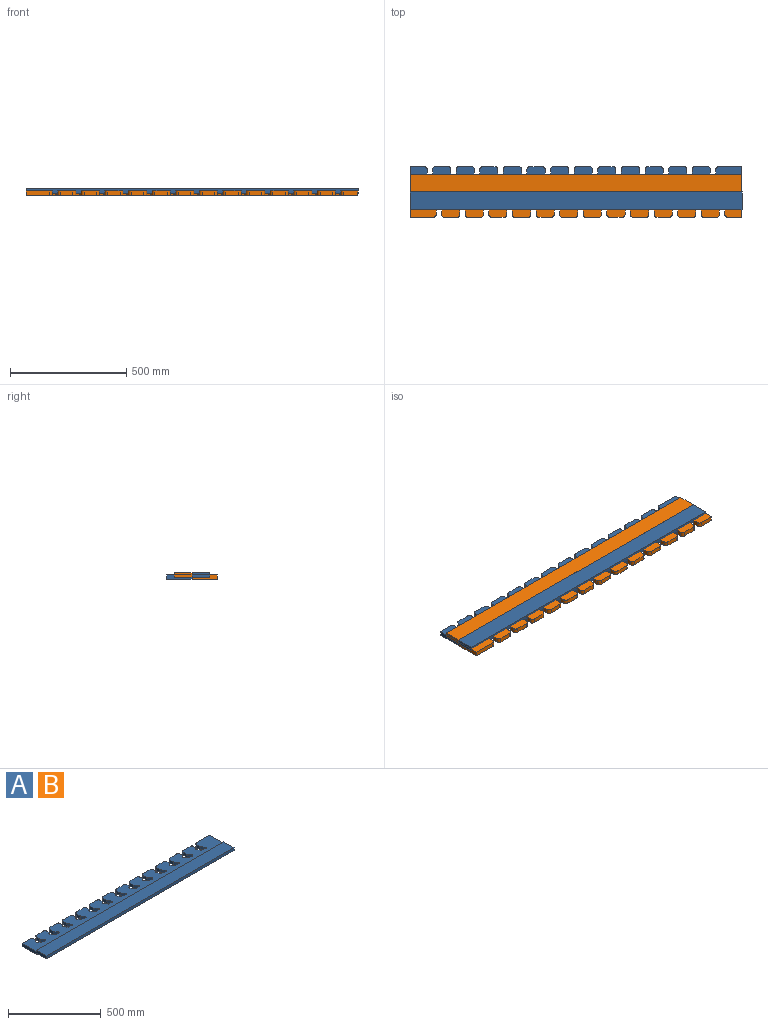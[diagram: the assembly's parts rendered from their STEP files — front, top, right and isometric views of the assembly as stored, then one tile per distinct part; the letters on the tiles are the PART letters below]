
ASSEMBLY  parts=2 mates=1
PART A: 208 faces, bbox 1428.8x185.4x28.6 mm
  f0: plane 52.88x19.05mm, normal (0,1,0), area 1007.4mm2, adj f1,f200,f201,f202
  f1: cylinder r=12.7mm len=19.05mm, axis (0,0,-1), area 380mm2, adj f0,f2,f201,f202
  f2: plane 25.53x19.05mm, normal (-1,0,0), area 486.4mm2, adj f1,f3,f201,f202
  f3: cylinder r=5.08mm len=19.05mm, axis (0,0,-1), area 70mm2, adj f2,f4,f201,f202
  f4: cylinder r=6.35mm len=19.05mm, axis (0,0,-1), area 12.4mm2, adj f3,f5,f201,f202
  f5: plane 20.02x19.05mm, normal (-0.81,-0.58,0), area 468.9mm2, adj f4,f6,f201,f202
  f6: cylinder r=6.35mm len=19.05mm, axis (0,0,-1), area 277mm2, adj f5,f7,f201,f202
  f7: plane 26.38x19.05mm, normal (0.1,1,0), area 504.9mm2, adj f6,f8,f201,f202
  f8: cylinder r=2.19mm len=19.05mm, axis (0,0,-1), area 35.6mm2, adj f7,f9,f201,f202
  f9: plane 21.55x19.05mm, normal (0.81,0.58,0), area 504.9mm2, adj f8,f10,f201,f202
  f10: cylinder r=6.35mm len=19.05mm, axis (0,0,-1), area 277mm2, adj f9,f11,f201,f202
  f11: plane 19.05x1.53mm, normal (0.1,1,0), area 29.2mm2, adj f10,f12,f201,f202
  f12: cylinder r=5.08mm len=19.05mm, axis (0,0,-1), area 161.5mm2, adj f11,f13,f201,f202
  f13: plane 19.18x19.05mm, normal (1,0,0), area 365.3mm2, adj f12,f14,f201,f202
  f14: cylinder r=12.7mm len=19.05mm, axis (0,0,-1), area 380mm2, adj f13,f15,f201,f202
  f15: plane 60.96x19.05mm, normal (0,1,0), area 1161.2mm2, adj f14,f16,f201,f202
  f16: plane 185.42x28.58mm, normal (-1,0,0), area 3532.3mm2, adj f15,f17,f201,f202,f203,f204,f206,f207
  f17: plane 1428.75x9.53mm, normal (0,-1,0), area 13608.8mm2, adj f16,f18,f202,f207
  f18: plane 109.22x19.05mm, normal (1,0,0), area 2080.6mm2, adj f17,f19,f201,f202,f203
  f19: plane 99.88x19.05mm, normal (0,1,0), area 1902.7mm2, adj f18,f20,f201,f202
  f20: cylinder r=12.7mm len=19.05mm, axis (0,0,-1), area 380mm2, adj f19,f21,f201,f202
  f21: plane 25.53x19.05mm, normal (-1,0,0), area 486.4mm2, adj f20,f22,f201,f202
  f22: cylinder r=5.08mm len=19.05mm, axis (0,0,-1), area 70mm2, adj f21,f23,f201,f202
  f23: cylinder r=6.35mm len=19.05mm, axis (0,0,-1), area 12.4mm2, adj f22,f24,f201,f202
  f24: plane 20.02x19.05mm, normal (-0.81,-0.58,0), area 468.9mm2, adj f23,f25,f201,f202
  f25: cylinder r=6.35mm len=19.05mm, axis (0,0,-1), area 277mm2, adj f24,f26,f201,f202
  f26: plane 26.38x19.05mm, normal (0.1,1,0), area 504.9mm2, adj f25,f27,f201,f202
  f27: cylinder r=2.19mm len=19.05mm, axis (0,0,-1), area 35.6mm2, adj f26,f28,f201,f202
  f28: plane 21.55x19.05mm, normal (0.81,0.58,0), area 504.9mm2, adj f27,f29,f201,f202
  f29: cylinder r=6.35mm len=19.05mm, axis (0,0,-1), area 277mm2, adj f28,f30,f201,f202
  f30: plane 19.05x1.53mm, normal (0.1,1,0), area 29.2mm2, adj f29,f31,f201,f202
  f31: cylinder r=5.08mm len=19.05mm, axis (0,0,-1), area 161.5mm2, adj f30,f32,f201,f202
  f32: plane 19.18x19.05mm, normal (1,0,0), area 365.3mm2, adj f31,f33,f201,f202
  f33: cylinder r=12.7mm len=19.05mm, axis (0,0,-1), area 380mm2, adj f32,f34,f201,f202
  f34: plane 52.88x19.05mm, normal (0,1,0), area 1007.4mm2, adj f33,f35,f201,f202
  f35: cylinder r=12.7mm len=19.05mm, axis (0,0,-1), area 380mm2, adj f34,f36,f201,f202
  f36: plane 25.53x19.05mm, normal (-1,0,0), area 486.4mm2, adj f35,f37,f201,f202
  f37: cylinder r=5.08mm len=19.05mm, axis (0,0,-1), area 70mm2, adj f36,f38,f201,f202
  f38: cylinder r=6.35mm len=19.05mm, axis (0,0,-1), area 12.4mm2, adj f37,f39,f201,f202
  f39: plane 20.02x19.05mm, normal (-0.81,-0.58,0), area 468.9mm2, adj f38,f40,f201,f202
  f40: cylinder r=6.35mm len=19.05mm, axis (0,0,-1), area 277mm2, adj f39,f41,f201,f202
  f41: plane 26.38x19.05mm, normal (0.1,1,0), area 504.9mm2, adj f40,f42,f201,f202
  f42: cylinder r=2.19mm len=19.05mm, axis (0,0,-1), area 35.6mm2, adj f41,f43,f201,f202
  f43: plane 21.55x19.05mm, normal (0.81,0.58,0), area 504.9mm2, adj f42,f44,f201,f202
  f44: cylinder r=6.35mm len=19.05mm, axis (0,0,-1), area 277mm2, adj f43,f45,f201,f202
  f45: plane 19.05x1.53mm, normal (0.1,1,0), area 29.2mm2, adj f44,f46,f201,f202
  f46: cylinder r=5.08mm len=19.05mm, axis (0,0,-1), area 161.5mm2, adj f45,f47,f201,f202
  f47: plane 19.18x19.05mm, normal (1,0,0), area 365.3mm2, adj f46,f48,f201,f202
  f48: cylinder r=12.7mm len=19.05mm, axis (0,0,-1), area 380mm2, adj f47,f49,f201,f202
  f49: plane 52.88x19.05mm, normal (0,1,0), area 1007.4mm2, adj f48,f50,f201,f202
  f50: cylinder r=12.7mm len=19.05mm, axis (0,0,-1), area 380mm2, adj f49,f51,f201,f202
  f51: plane 25.53x19.05mm, normal (-1,0,0), area 486.4mm2, adj f50,f52,f201,f202
  f52: cylinder r=5.08mm len=19.05mm, axis (0,0,-1), area 70mm2, adj f51,f53,f201,f202
  f53: cylinder r=6.35mm len=19.05mm, axis (0,0,-1), area 12.4mm2, adj f52,f54,f201,f202
  f54: plane 20.02x19.05mm, normal (-0.81,-0.58,0), area 468.9mm2, adj f53,f55,f201,f202
  f55: cylinder r=6.35mm len=19.05mm, axis (0,0,-1), area 277mm2, adj f54,f56,f201,f202
  f56: plane 26.38x19.05mm, normal (0.1,1,0), area 504.9mm2, adj f55,f57,f201,f202
  f57: cylinder r=2.19mm len=19.05mm, axis (0,0,-1), area 35.6mm2, adj f56,f58,f201,f202
  f58: plane 21.55x19.05mm, normal (0.81,0.58,0), area 504.9mm2, adj f57,f59,f201,f202
  f59: cylinder r=6.35mm len=19.05mm, axis (0,0,-1), area 277mm2, adj f58,f60,f201,f202
  f60: plane 19.05x1.53mm, normal (0.1,1,0), area 29.2mm2, adj f59,f61,f201,f202
  f61: cylinder r=5.08mm len=19.05mm, axis (0,0,-1), area 161.5mm2, adj f60,f62,f201,f202
  f62: plane 19.18x19.05mm, normal (1,0,0), area 365.3mm2, adj f61,f63,f201,f202
  f63: cylinder r=12.7mm len=19.05mm, axis (0,0,-1), area 380mm2, adj f62,f64,f201,f202
  f64: plane 52.88x19.05mm, normal (0,1,0), area 1007.4mm2, adj f63,f65,f201,f202
  f65: cylinder r=12.7mm len=19.05mm, axis (0,0,-1), area 380mm2, adj f64,f66,f201,f202
  f66: plane 25.53x19.05mm, normal (-1,0,0), area 486.4mm2, adj f65,f67,f201,f202
  f67: cylinder r=5.08mm len=19.05mm, axis (0,0,-1), area 70mm2, adj f66,f68,f201,f202
  f68: cylinder r=6.35mm len=19.05mm, axis (0,0,-1), area 12.4mm2, adj f67,f69,f201,f202
  f69: plane 20.02x19.05mm, normal (-0.81,-0.58,0), area 468.9mm2, adj f68,f70,f201,f202
  f70: cylinder r=6.35mm len=19.05mm, axis (0,0,-1), area 277mm2, adj f69,f71,f201,f202
  f71: plane 26.38x19.05mm, normal (0.1,1,0), area 504.9mm2, adj f70,f72,f201,f202
  f72: cylinder r=2.19mm len=19.05mm, axis (0,0,-1), area 35.6mm2, adj f71,f73,f201,f202
  f73: plane 21.55x19.05mm, normal (0.81,0.58,0), area 504.9mm2, adj f72,f74,f201,f202
  f74: cylinder r=6.35mm len=19.05mm, axis (0,0,-1), area 277mm2, adj f73,f75,f201,f202
  f75: plane 19.05x1.53mm, normal (0.1,1,0), area 29.2mm2, adj f74,f76,f201,f202
  f76: cylinder r=5.08mm len=19.05mm, axis (0,0,-1), area 161.5mm2, adj f75,f77,f201,f202
  f77: plane 19.18x19.05mm, normal (1,0,0), area 365.3mm2, adj f76,f78,f201,f202
  f78: cylinder r=12.7mm len=19.05mm, axis (0,0,-1), area 380mm2, adj f77,f79,f201,f202
  f79: plane 52.88x19.05mm, normal (0,1,0), area 1007.4mm2, adj f78,f80,f201,f202
  f80: cylinder r=12.7mm len=19.05mm, axis (0,0,-1), area 380mm2, adj f79,f81,f201,f202
  f81: plane 25.53x19.05mm, normal (-1,0,0), area 486.4mm2, adj f80,f82,f201,f202
  f82: cylinder r=5.08mm len=19.05mm, axis (0,0,-1), area 70mm2, adj f81,f83,f201,f202
  f83: cylinder r=6.35mm len=19.05mm, axis (0,0,-1), area 12.4mm2, adj f82,f84,f201,f202
  f84: plane 20.02x19.05mm, normal (-0.81,-0.58,0), area 468.9mm2, adj f83,f85,f201,f202
  f85: cylinder r=6.35mm len=19.05mm, axis (0,0,-1), area 277mm2, adj f84,f86,f201,f202
  f86: plane 26.38x19.05mm, normal (0.1,1,0), area 504.9mm2, adj f85,f87,f201,f202
  f87: cylinder r=2.19mm len=19.05mm, axis (0,0,-1), area 35.6mm2, adj f86,f88,f201,f202
  f88: plane 21.55x19.05mm, normal (0.81,0.58,0), area 504.9mm2, adj f87,f89,f201,f202
  f89: cylinder r=6.35mm len=19.05mm, axis (0,0,-1), area 277mm2, adj f88,f90,f201,f202
  f90: plane 19.05x1.53mm, normal (0.1,1,0), area 29.2mm2, adj f89,f91,f201,f202
  f91: cylinder r=5.08mm len=19.05mm, axis (0,0,-1), area 161.5mm2, adj f90,f92,f201,f202
  f92: plane 19.18x19.05mm, normal (1,0,0), area 365.3mm2, adj f91,f93,f201,f202
  f93: cylinder r=12.7mm len=19.05mm, axis (0,0,-1), area 380mm2, adj f92,f94,f201,f202
  f94: plane 52.88x19.05mm, normal (0,1,0), area 1007.4mm2, adj f93,f95,f201,f202
  f95: cylinder r=12.7mm len=19.05mm, axis (0,0,-1), area 380mm2, adj f94,f96,f201,f202
  f96: plane 25.53x19.05mm, normal (-1,0,0), area 486.4mm2, adj f95,f97,f201,f202
  f97: cylinder r=5.08mm len=19.05mm, axis (0,0,-1), area 70mm2, adj f96,f98,f201,f202
  f98: cylinder r=6.35mm len=19.05mm, axis (0,0,-1), area 12.4mm2, adj f97,f99,f201,f202
  f99: plane 20.02x19.05mm, normal (-0.81,-0.58,0), area 468.9mm2, adj f98,f100,f201,f202
  f100: cylinder r=6.35mm len=19.05mm, axis (0,0,-1), area 277mm2, adj f99,f101,f201,f202
  f101: plane 26.38x19.05mm, normal (0.1,1,0), area 504.9mm2, adj f100,f102,f201,f202
  f102: cylinder r=2.19mm len=19.05mm, axis (0,0,-1), area 35.6mm2, adj f101,f103,f201,f202
  f103: plane 21.55x19.05mm, normal (0.81,0.58,0), area 504.9mm2, adj f102,f104,f201,f202
  f104: cylinder r=6.35mm len=19.05mm, axis (0,0,-1), area 277mm2, adj f103,f105,f201,f202
  f105: plane 19.05x1.53mm, normal (0.1,1,0), area 29.2mm2, adj f104,f106,f201,f202
  f106: cylinder r=5.08mm len=19.05mm, axis (0,0,-1), area 161.5mm2, adj f105,f107,f201,f202
  f107: plane 19.18x19.05mm, normal (1,0,0), area 365.3mm2, adj f106,f108,f201,f202
  f108: cylinder r=12.7mm len=19.05mm, axis (0,0,-1), area 380mm2, adj f107,f109,f201,f202
  f109: plane 52.88x19.05mm, normal (0,1,0), area 1007.4mm2, adj f108,f110,f201,f202
  f110: cylinder r=12.7mm len=19.05mm, axis (0,0,-1), area 380mm2, adj f109,f111,f201,f202
  f111: plane 25.53x19.05mm, normal (-1,0,0), area 486.4mm2, adj f110,f112,f201,f202
  f112: cylinder r=5.08mm len=19.05mm, axis (0,0,-1), area 70mm2, adj f111,f113,f201,f202
  f113: cylinder r=6.35mm len=19.05mm, axis (0,0,-1), area 12.4mm2, adj f112,f114,f201,f202
  f114: plane 20.02x19.05mm, normal (-0.81,-0.58,0), area 468.9mm2, adj f113,f115,f201,f202
  f115: cylinder r=6.35mm len=19.05mm, axis (0,0,-1), area 277mm2, adj f114,f116,f201,f202
  f116: plane 26.38x19.05mm, normal (0.1,1,0), area 504.9mm2, adj f115,f117,f201,f202
  f117: cylinder r=2.19mm len=19.05mm, axis (0,0,-1), area 35.6mm2, adj f116,f118,f201,f202
  f118: plane 21.55x19.05mm, normal (0.81,0.58,0), area 504.9mm2, adj f117,f119,f201,f202
  f119: cylinder r=6.35mm len=19.05mm, axis (0,0,-1), area 277mm2, adj f118,f120,f201,f202
  f120: plane 19.05x1.53mm, normal (0.1,1,0), area 29.2mm2, adj f119,f121,f201,f202
  f121: cylinder r=5.08mm len=19.05mm, axis (0,0,-1), area 161.5mm2, adj f120,f122,f201,f202
  f122: plane 19.18x19.05mm, normal (1,0,0), area 365.3mm2, adj f121,f123,f201,f202
  f123: extruded ~19.05x7.08mm, area 141.2mm2, adj f122,f124,f201,f202
  f124: cylinder r=12.7mm len=19.05mm, axis (0,0,-1), area 229.2mm2, adj f123,f125,f201,f202
  f125: extruded ~19.05x0.41mm, area 7.7mm2, adj f124,f126,f201,f202
  f126: plane 52.88x19.05mm, normal (0,1,0), area 1007.4mm2, adj f125,f127,f201,f202
  f127: cylinder r=12.7mm len=19.05mm, axis (0,0,-1), area 380mm2, adj f126,f128,f201,f202
  f128: plane 25.53x19.05mm, normal (-1,0,0), area 486.4mm2, adj f127,f129,f201,f202
  f129: cylinder r=5.08mm len=19.05mm, axis (0,0,-1), area 70mm2, adj f128,f130,f201,f202
  f130: cylinder r=6.35mm len=19.05mm, axis (0,0,-1), area 12.4mm2, adj f129,f131,f201,f202
  f131: plane 20.02x19.05mm, normal (-0.81,-0.58,0), area 468.9mm2, adj f130,f132,f201,f202
  f132: cylinder r=6.35mm len=19.05mm, axis (0,0,-1), area 277mm2, adj f131,f133,f201,f202
  f133: plane 26.38x19.05mm, normal (0.1,1,0), area 504.9mm2, adj f132,f134,f201,f202
  f134: cylinder r=2.19mm len=19.05mm, axis (0,0,-1), area 35.6mm2, adj f133,f135,f201,f202
  f135: plane 21.55x19.05mm, normal (0.81,0.58,0), area 504.9mm2, adj f134,f136,f201,f202
  f136: cylinder r=6.35mm len=19.05mm, axis (0,0,-1), area 277mm2, adj f135,f137,f201,f202
  f137: plane 19.05x1.53mm, normal (0.1,1,0), area 29.2mm2, adj f136,f138,f201,f202
  f138: cylinder r=5.08mm len=19.05mm, axis (0,0,-1), area 161.5mm2, adj f137,f139,f201,f202
  f139: plane 19.18x19.05mm, normal (1,0,0), area 365.3mm2, adj f138,f140,f201,f202
  f140: cylinder r=12.7mm len=19.05mm, axis (0,0,-1), area 380mm2, adj f139,f141,f201,f202
  f141: plane 52.88x19.05mm, normal (0,1,0), area 1007.4mm2, adj f140,f142,f201,f202
  f142: cylinder r=12.7mm len=19.05mm, axis (0,0,-1), area 380mm2, adj f141,f143,f201,f202
  f143: plane 25.53x19.05mm, normal (-1,0,0), area 486.4mm2, adj f142,f144,f201,f202
  f144: cylinder r=5.08mm len=19.05mm, axis (0,0,-1), area 70mm2, adj f143,f145,f201,f202
  f145: cylinder r=6.35mm len=19.05mm, axis (0,0,-1), area 12.4mm2, adj f144,f146,f201,f202
  f146: plane 20.02x19.05mm, normal (-0.81,-0.58,0), area 468.9mm2, adj f145,f147,f201,f202
  f147: cylinder r=6.35mm len=19.05mm, axis (0,0,-1), area 277mm2, adj f146,f148,f201,f202
  f148: plane 26.38x19.05mm, normal (0.1,1,0), area 504.9mm2, adj f147,f149,f201,f202
  f149: cylinder r=2.19mm len=19.05mm, axis (0,0,-1), area 35.6mm2, adj f148,f150,f201,f202
  f150: plane 21.55x19.05mm, normal (0.81,0.58,0), area 504.9mm2, adj f149,f151,f201,f202
  f151: cylinder r=6.35mm len=19.05mm, axis (0,0,-1), area 277mm2, adj f150,f152,f201,f202
  f152: plane 19.05x1.53mm, normal (0.1,1,0), area 29.2mm2, adj f151,f153,f201,f202
  f153: cylinder r=5.08mm len=19.05mm, axis (0,0,-1), area 161.5mm2, adj f152,f154,f201,f202
  f154: plane 19.18x19.05mm, normal (1,0,0), area 365.3mm2, adj f153,f155,f201,f202
  f155: cylinder r=12.7mm len=19.05mm, axis (0,0,-1), area 380mm2, adj f154,f156,f201,f202
  f156: plane 52.88x19.05mm, normal (0,1,0), area 1007.4mm2, adj f155,f157,f201,f202
  f157: cylinder r=12.7mm len=19.05mm, axis (0,0,-1), area 380mm2, adj f156,f158,f201,f202
  f158: plane 25.53x19.05mm, normal (-1,0,0), area 486.4mm2, adj f157,f159,f201,f202
  f159: cylinder r=5.08mm len=19.05mm, axis (0,0,-1), area 70mm2, adj f158,f160,f201,f202
  f160: cylinder r=6.35mm len=19.05mm, axis (0,0,-1), area 12.4mm2, adj f159,f161,f201,f202
  f161: plane 20.02x19.05mm, normal (-0.81,-0.58,0), area 468.9mm2, adj f160,f162,f201,f202
  f162: cylinder r=6.35mm len=19.05mm, axis (0,0,-1), area 277mm2, adj f161,f163,f201,f202
  f163: plane 26.38x19.05mm, normal (0.1,1,0), area 504.9mm2, adj f162,f164,f201,f202
  f164: cylinder r=2.19mm len=19.05mm, axis (0,0,-1), area 35.6mm2, adj f163,f165,f201,f202
  f165: plane 21.55x19.05mm, normal (0.81,0.58,0), area 504.9mm2, adj f164,f166,f201,f202
  f166: cylinder r=6.35mm len=19.05mm, axis (0,0,-1), area 277mm2, adj f165,f167,f201,f202
  f167: plane 19.05x1.53mm, normal (0.1,1,0), area 29.2mm2, adj f166,f168,f201,f202
  f168: cylinder r=5.08mm len=19.05mm, axis (0,0,-1), area 161.5mm2, adj f167,f169,f201,f202
  f169: plane 19.18x19.05mm, normal (1,0,0), area 365.3mm2, adj f168,f170,f201,f202
  f170: cylinder r=12.7mm len=19.05mm, axis (0,0,-1), area 380mm2, adj f169,f171,f201,f202
  f171: plane 52.88x19.05mm, normal (0,1,0), area 1007.4mm2, adj f170,f172,f201,f202
  f172: cylinder r=12.7mm len=19.05mm, axis (0,0,-1), area 380mm2, adj f171,f173,f201,f202
  f173: plane 25.53x19.05mm, normal (-1,0,0), area 486.4mm2, adj f172,f174,f201,f202
  f174: cylinder r=5.08mm len=19.05mm, axis (0,0,-1), area 70mm2, adj f173,f175,f201,f202
  f175: cylinder r=6.35mm len=19.05mm, axis (0,0,-1), area 12.4mm2, adj f174,f176,f201,f202
  f176: plane 20.02x19.05mm, normal (-0.81,-0.58,0), area 468.9mm2, adj f175,f177,f201,f202
  f177: cylinder r=6.35mm len=19.05mm, axis (0,0,-1), area 277mm2, adj f176,f178,f201,f202
  f178: plane 26.38x19.05mm, normal (0.1,1,0), area 504.9mm2, adj f177,f179,f201,f202
  f179: cylinder r=2.19mm len=19.05mm, axis (0,0,-1), area 35.6mm2, adj f178,f180,f201,f202
  f180: plane 21.55x19.05mm, normal (0.81,0.58,0), area 504.9mm2, adj f179,f181,f201,f202
  f181: cylinder r=6.35mm len=19.05mm, axis (0,0,-1), area 277mm2, adj f180,f182,f201,f202
  f182: plane 19.05x1.53mm, normal (0.1,1,0), area 29.2mm2, adj f181,f183,f201,f202
  f183: cylinder r=5.08mm len=19.05mm, axis (0,0,-1), area 161.5mm2, adj f182,f184,f201,f202
  f184: plane 19.18x19.05mm, normal (1,0,0), area 365.3mm2, adj f183,f185,f201,f202
  f185: cylinder r=12.7mm len=19.05mm, axis (0,0,-1), area 380mm2, adj f184,f186,f201,f202
  f186: plane 52.88x19.05mm, normal (0,1,0), area 1007.4mm2, adj f185,f187,f201,f202
  f187: cylinder r=12.7mm len=19.05mm, axis (0,0,-1), area 380mm2, adj f186,f188,f201,f202
  f188: plane 25.53x19.05mm, normal (-1,0,0), area 486.4mm2, adj f187,f189,f201,f202
  f189: cylinder r=5.08mm len=19.05mm, axis (0,0,-1), area 70mm2, adj f188,f190,f201,f202
  f190: cylinder r=6.35mm len=19.05mm, axis (0,0,-1), area 12.4mm2, adj f189,f191,f201,f202
  f191: plane 20.02x19.05mm, normal (-0.81,-0.58,0), area 468.9mm2, adj f190,f192,f201,f202
  f192: cylinder r=6.35mm len=19.05mm, axis (0,0,-1), area 277mm2, adj f191,f193,f201,f202
  f193: plane 26.38x19.05mm, normal (0.1,1,0), area 504.9mm2, adj f192,f194,f201,f202
  f194: cylinder r=2.19mm len=19.05mm, axis (0,0,-1), area 35.6mm2, adj f193,f195,f201,f202
  f195: plane 21.55x19.05mm, normal (0.81,0.58,0), area 504.9mm2, adj f194,f196,f201,f202
  f196: cylinder r=6.35mm len=19.05mm, axis (0,0,-1), area 277mm2, adj f195,f197,f201,f202
  f197: plane 19.05x1.53mm, normal (0.1,1,0), area 29.2mm2, adj f196,f198,f201,f202
  f198: cylinder r=5.08mm len=19.05mm, axis (0,0,-1), area 161.5mm2, adj f197,f199,f201,f202
  f199: plane 19.18x19.05mm, normal (1,0,0), area 365.3mm2, adj f198,f200,f201,f202
  f200: cylinder r=12.7mm len=19.05mm, axis (0,0,-1), area 380mm2, adj f0,f199,f201,f202
  f201: plane 1428.75x109.22mm, normal (0,0,1), area 127617.5mm2, adj f0,f1,f2,f3,f4,f5,f6,f7
  f202: plane 1428.75x109.22mm, normal (0,0,-1), area 127617.5mm2, adj f0,f1,f2,f3,f4,f5,f6,f7
  f203: plane 1428.84x19.05mm, normal (0,1,0), area 13610.6mm2, adj f16,f18,f201,f205,f206,f207
  f204: plane 1428.84x19.05mm, normal (0,-1,0), area 27219.5mm2, adj f16,f205,f206,f207
  f205: plane 76.2x19.05mm, normal (1,0,0), area 1451.6mm2, adj f203,f204,f206,f207
  f206: plane 1428.84x76.2mm, normal (0,0,1), area 108877.8mm2, adj f16,f203,f204,f205
  f207: plane 1428.84x76.2mm, normal (0,0,-1), area 108877.8mm2, adj f16,f17,f203,f204,f205
PART B: same geometry as A
PLACE A t=(-1072,96.61,-94.04)mm
PLACE B rot(axis=(0,0,-1),180deg) t=(356.75,96.61,-94.04)mm
MATE planar A.f203 <-> B.f203  axis (0,-1,0) through (356.75,96.61,-84.51)mm
